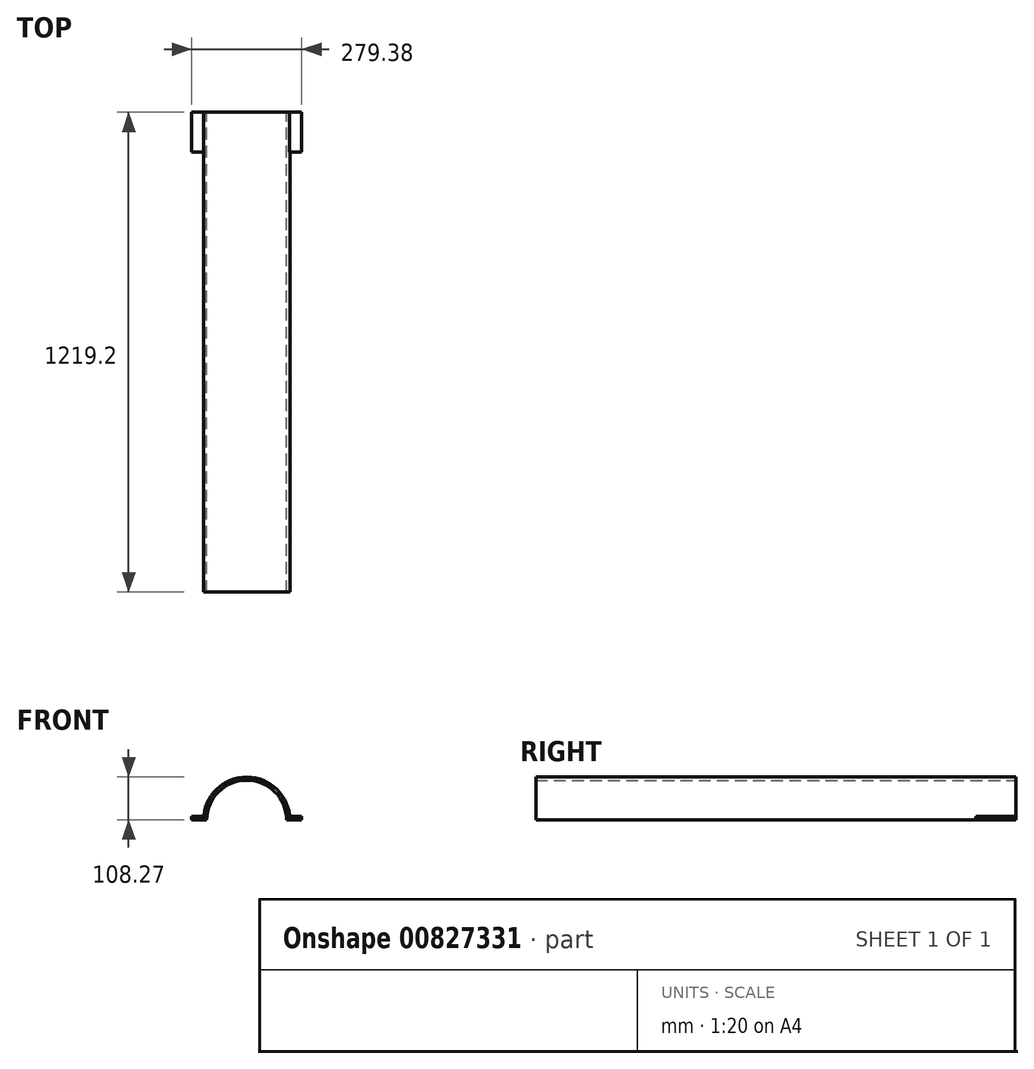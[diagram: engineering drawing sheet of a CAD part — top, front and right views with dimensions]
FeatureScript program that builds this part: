
annotation { "Feature Type Name" : "Feature", "Feature Type Description" : "" }
export const myFeature = defineFeature(function(context is Context, id is Id, definition is map)
    precondition{}
    {
        {
            var Q0;
            Q0=qCreatedBy(makeId("Front.planeOp"),FACE);
            var sketch = newSketch(context, id + "F0", { "sketchPlane" : qUnion([Q0])});
            skLineSegment(sketch, "E0.bottom", {"start": v(127, -1.27) * mm, "end": v(-127, -1.27) * mm});
            skLineSegment(sketch, "E0.top", {"start": v(127, 1.27) * mm, "end": v(-127, 1.27) * mm});
            skLineSegment(sketch, "E0.left", {"start": v(127, -1.27) * mm, "end": v(127, 1.27) * mm});
            skLineSegment(sketch, "E0.right", {"start": v(-127, -1.27) * mm, "end": v(-127, 1.27) * mm});
            skPoint(sketch, "E0.middle", {"position": v(0, 0) * mm});
            skArc(sketch, "E1.trimOffspring", {"start": v(101.6, 1.27) * mm, "mid": v(0, 101.6) * mm, "end": v(-101.6, 1.27) * mm});
            skArc(sketch, "E2.trimOffspring", {"start": v(109.53, 1.27) * mm, "mid": v(0, 109.54) * mm, "end": v(-109.53, 1.27) * mm});
            skLineSegment(sketch, "E3.bottom", {"start": v(-101.6, 1.27) * mm, "end": v(-139.7, 1.27) * mm});
            skLineSegment(sketch, "E3.top", {"start": v(-109.13, 9.45) * mm, "end": v(-139.7, 9.45) * mm});
            skLineSegment(sketch, "E3.right", {"start": v(-139.7, 1.27) * mm, "end": v(-139.7, 9.45) * mm});
            skLineSegment(sketch, "E4", {"start": v(0, 0) * mm, "end": v(0, 50.99) * mm});
            skLineSegment(sketch, "E5.MirrorCS", {"start": v(101.6, 1.27) * mm, "end": v(139.7, 1.27) * mm});
            skLineSegment(sketch, "E6.MirrorCS", {"start": v(139.7, 1.27) * mm, "end": v(139.7, 9.45) * mm});
            skLineSegment(sketch, "E7.MirrorCS", {"start": v(109.13, 9.45) * mm, "end": v(139.7, 9.45) * mm});
            skPoint(sketch, "E3.left.end.orphan", {"position": v(-101.6, 9.45) * mm});
            skPoint(sketch, "E8.MirrorCS.end.orphan", {"position": v(101.6, 9.45) * mm});
            skPoint(sketch, "E8.MirrorCS.start.orphan", {"position": v(101.6, 1.27) * mm});
            skSolve(sketch);
        }
        {
            var Q0;
            {var subQ0=sQuery(id+"F0.wireOp",EDGE,"E1.trimOffspring");Q0=makeQuery(id+"F0.imprint","IMPRINT",FACE,{"disambiguationData":[TD([[makeQuery(id+"F0.imprint","IMPRINT",EDGE,{"derivedFrom":subQ0}),-1.0]])]});}
            extrude(context, id + "F1", {"entities" : qUnion([Q0]), "depth" : 1219.2 * mm, "offsetDistance" : 25.4 * mm});
        }
        {
            var Q0;
            {var subQ0=sQuery(id+"F0.wireOp",EDGE,"E3.top");Q0=makeQuery(id+"F0.imprint","IMPRINT",FACE,{"disambiguationData":[TD([[makeQuery(id+"F0.imprint","IMPRINT",EDGE,{"derivedFrom":subQ0}),1.0]])]});}
            var Q1;
            {var subQ0=sQuery(id+"F0.wireOp",EDGE,"E6.MirrorCS");Q1=makeQuery(id+"F0.imprint","IMPRINT",FACE,{"disambiguationData":[TD([[makeQuery(id+"F0.imprint","IMPRINT",EDGE,{"derivedFrom":subQ0}),1.0]])]});}
            extrude(context, id + "F2", {"entities" : qUnion([Q0, Q1]), "operationType" : NewBodyOperationType.ADD, "depth" : 101.6 * mm, "offsetDistance" : 25.4 * mm});
        }
    });
